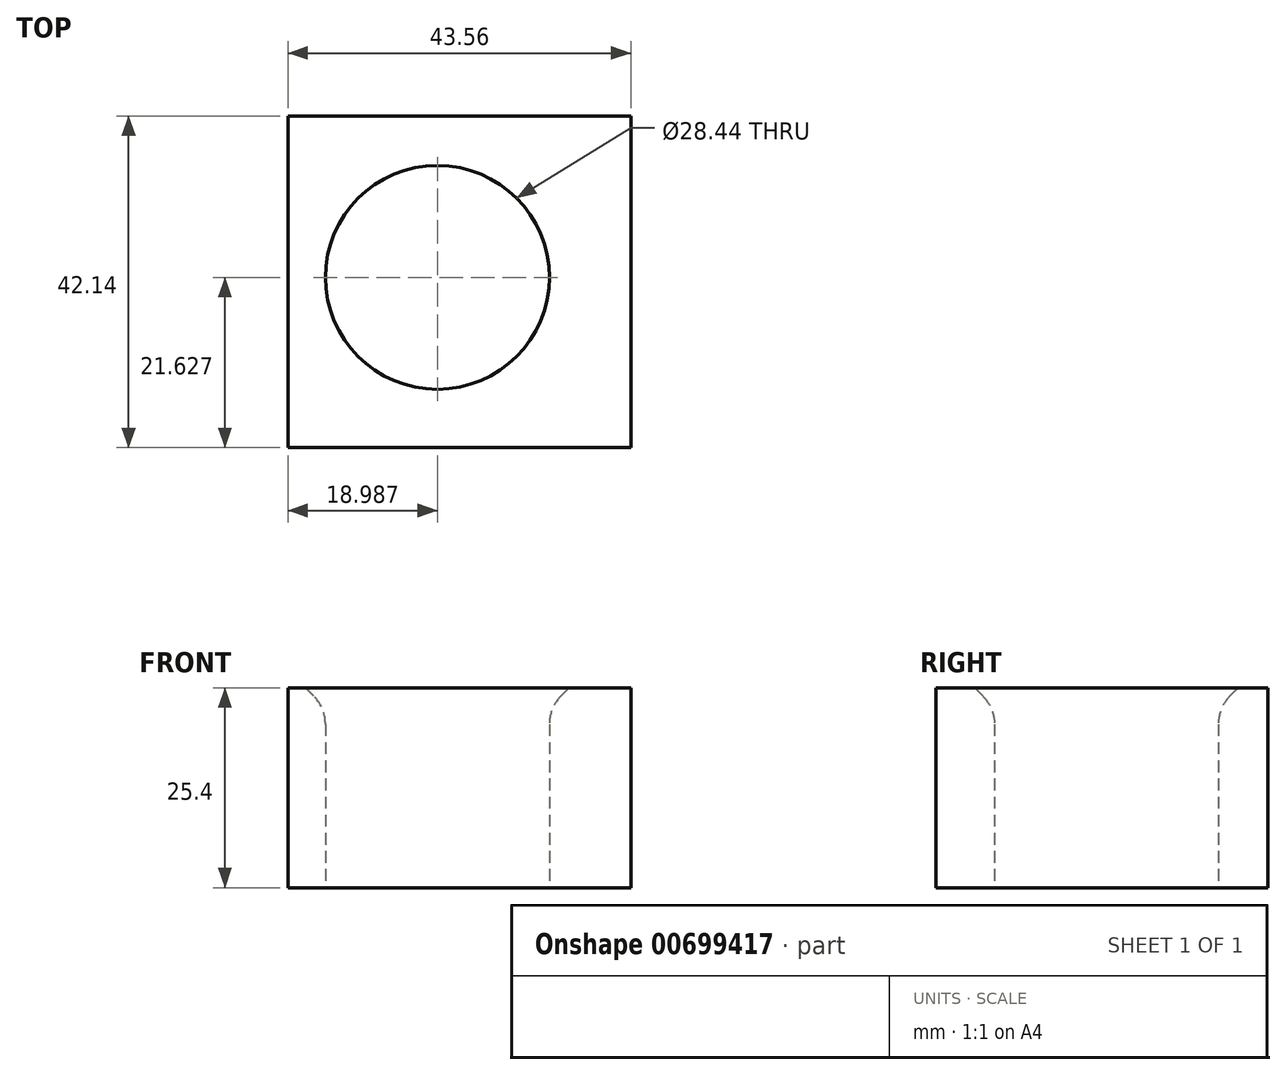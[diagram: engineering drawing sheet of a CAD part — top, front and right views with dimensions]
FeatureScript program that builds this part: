
annotation { "Feature Type Name" : "Feature", "Feature Type Description" : "" }
export const myFeature = defineFeature(function(context is Context, id is Id, definition is map)
    precondition{}
    {
        {
            var Q0;
            Q0=qCreatedBy(makeId("Top.planeOp"),FACE);
            var sketch = newSketch(context, id + "F0", { "sketchPlane" : qUnion([Q0])});
            skLineSegment(sketch, "E0.bottom", {"start": v(0, 0) * mm, "end": v(43.56, 0) * mm});
            skLineSegment(sketch, "E0.top", {"start": v(0, 42.14) * mm, "end": v(43.56, 42.14) * mm});
            skLineSegment(sketch, "E0.left", {"start": v(0, 0) * mm, "end": v(0, 42.14) * mm});
            skLineSegment(sketch, "E0.right", {"start": v(43.56, 0) * mm, "end": v(43.56, 42.14) * mm});
            skCircle(sketch, "E1", {"center": v(18.99, 21.63) * mm, "radius": 14.22 * mm});
            skSolve(sketch);
        }
        {
            var Q0;
            Q0=makeQuery(id+"F0.imprint","IMPRINT",FACE,{"disambiguationData":[TD([[makeQuery(id+"F0.imprint","IMPRINT",EDGE,{"derivedFrom":sQuery(id+"F0.wireOp",EDGE,"E0.bottom")}),1.0]])]});
            extrude(context, id + "F1", {"entities" : qUnion([Q0]), "depth" : 25.4 * mm, "offsetDistance" : 25.4 * mm});
        }
        {
            var Q0;
            Q0=makeQuery(id+"F1.opExtrude","CAP_EDGE",EDGE,{"disambiguationData":[OSD([sQuery(id+"F0.wireOp",EDGE,"E1")])],"isStart":false});
            chamfer(context, id + "F2", {"entities" : qUnion([Q0]), "width" : 2.54 * mm, "tangentPropagation" : true});
        }
        {
            var Q0;
            {var subQ0=sQuery(id+"F0.wireOp",EDGE,"E1");Q0=makeQuery(id+"F2.opChamfer","BLEND_EDGE",EDGE,{"blendedFrom":[makeQuery(id+"F1.opExtrude","CAP_EDGE",EDGE,{"disambiguationData":[OSD([subQ0])],"isStart":false}),makeQuery(id+"F1.opExtrude","CAP_FACE",FACE,{"disambiguationData":[OSD([sQuery(id+"F0.wireOp",EDGE,"E0.bottom"),sQuery(id+"F0.wireOp",EDGE,"E0.top"),sQuery(id+"F0.wireOp",EDGE,"E0.left"),sQuery(id+"F0.wireOp",EDGE,"E0.right"),subQ0])],"isStart":false})],"blendedInto":[makeQuery(id+"F1.opExtrude","CAP_FACE",FACE,{"disambiguationData":[OSD([sQuery(id+"F0.wireOp",EDGE,"E0.bottom"),sQuery(id+"F0.wireOp",EDGE,"E0.top"),sQuery(id+"F0.wireOp",EDGE,"E0.left"),sQuery(id+"F0.wireOp",EDGE,"E0.right"),subQ0])],"isStart":false})]});}
            fillet(context, id + "F3", {"entities" : qUnion([Q0]), "radius" : 0.76 * mm, "tangentPropagation" : true, "allowEdgeOverflow" : false});
        }
        {
            var Q0;
            {var subQ0=sQuery(id+"F0.wireOp",EDGE,"E1");Q0=makeQuery(id+"F2.opChamfer","BLEND_EDGE",EDGE,{"blendedFrom":[makeQuery(id+"F1.opExtrude","CAP_EDGE",EDGE,{"disambiguationData":[OSD([subQ0])],"isStart":false}),makeQuery(id+"F1.opExtrude","SWEPT_FACE",FACE,{"disambiguationData":[OSD([subQ0])]})],"blendedInto":[makeQuery(id+"F1.opExtrude","SWEPT_FACE",FACE,{"disambiguationData":[OSD([subQ0])]})]});}
            fillet(context, id + "F4", {"entities" : qUnion([Q0]), "radius" : 5.08 * mm, "tangentPropagation" : true, "allowEdgeOverflow" : false});
        }
    });
